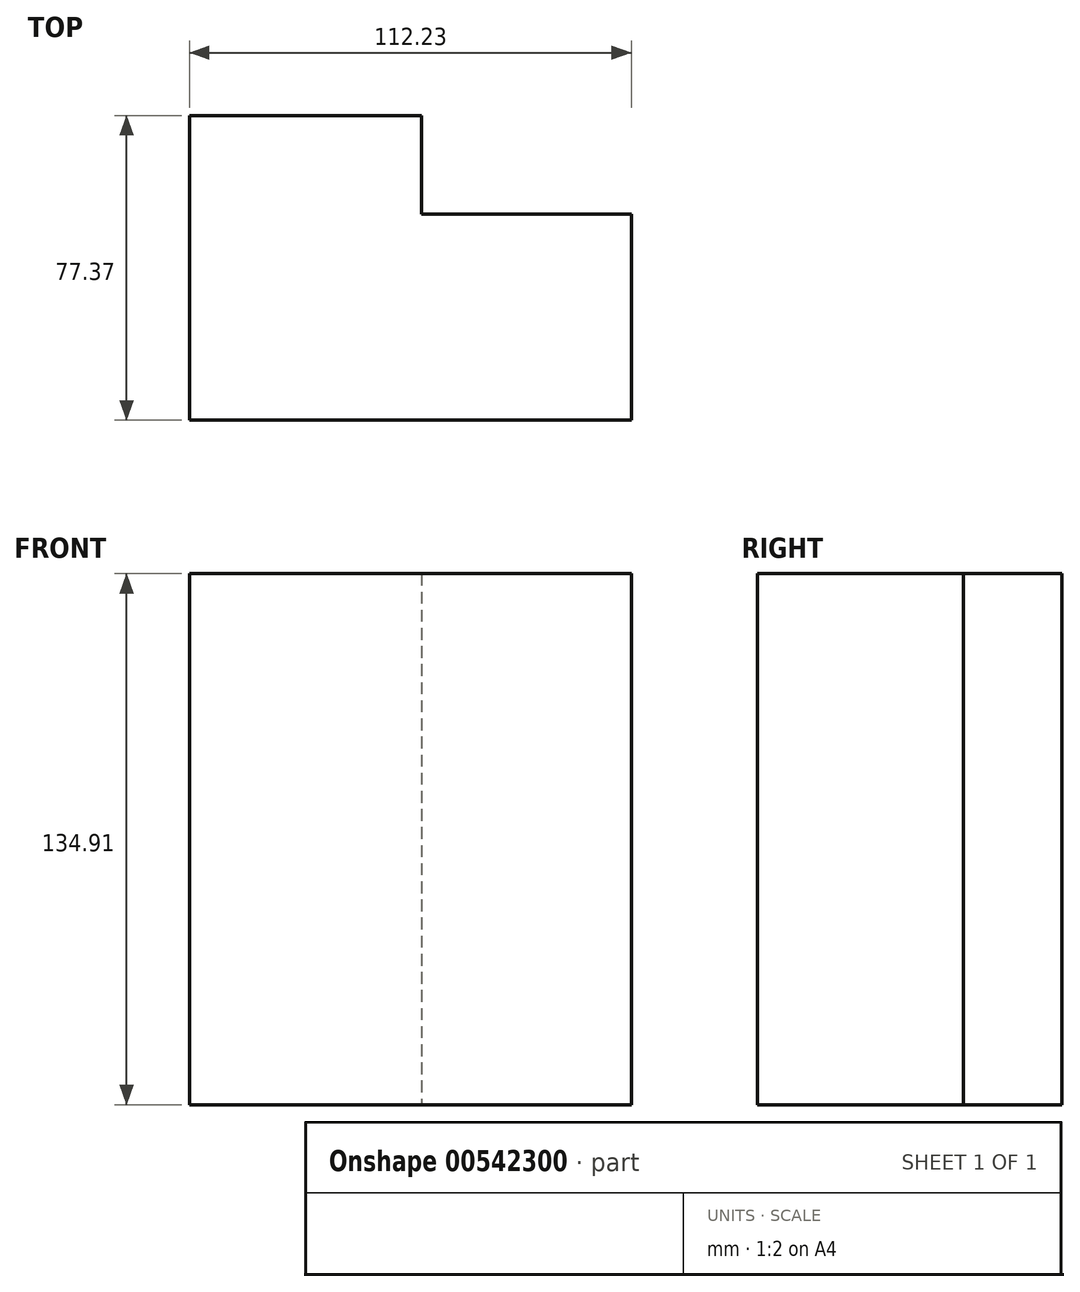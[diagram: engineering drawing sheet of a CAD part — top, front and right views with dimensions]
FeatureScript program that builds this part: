
annotation { "Feature Type Name" : "Feature", "Feature Type Description" : "" }
export const myFeature = defineFeature(function(context is Context, id is Id, definition is map)
    precondition{}
    {
        {
            var Q0;
            Q0=qCreatedBy(makeId("Top.planeOp"),FACE);
            var sketch = newSketch(context, id + "F0", { "sketchPlane" : qUnion([Q0])});
            skLineSegment(sketch, "E0.bottom", {"start": v(-53.28, 52.32) * mm, "end": v(0, 52.32) * mm});
            skLineSegment(sketch, "E0.top", {"start": v(-53.28, 0) * mm, "end": v(0, 0) * mm});
            skLineSegment(sketch, "E0.left", {"start": v(-53.28, 52.32) * mm, "end": v(-53.28, 0) * mm});
            skLineSegment(sketch, "E0.right", {"start": v(0, 52.32) * mm, "end": v(0, 0) * mm});
            skLineSegment(sketch, "E1.bottom", {"start": v(-53.28, 0) * mm, "end": v(-112.23, 0) * mm});
            skLineSegment(sketch, "E1.top", {"start": v(-53.28, 77.37) * mm, "end": v(-112.23, 77.37) * mm});
            skLineSegment(sketch, "E1.left", {"start": v(-53.28, 0) * mm, "end": v(-53.28, 77.37) * mm});
            skLineSegment(sketch, "E1.right", {"start": v(-112.23, 0) * mm, "end": v(-112.23, 77.37) * mm});
            skSolve(sketch);
        }
        {
            var Q0;
            Q0 = qSketchRegion(id + "F0", true);
            extrude(context, id + "F1", {"entities" : qUnion([Q0]), "depth" : 134.9 * mm, "offsetDistance" : 25.4 * mm});
        }
    });
